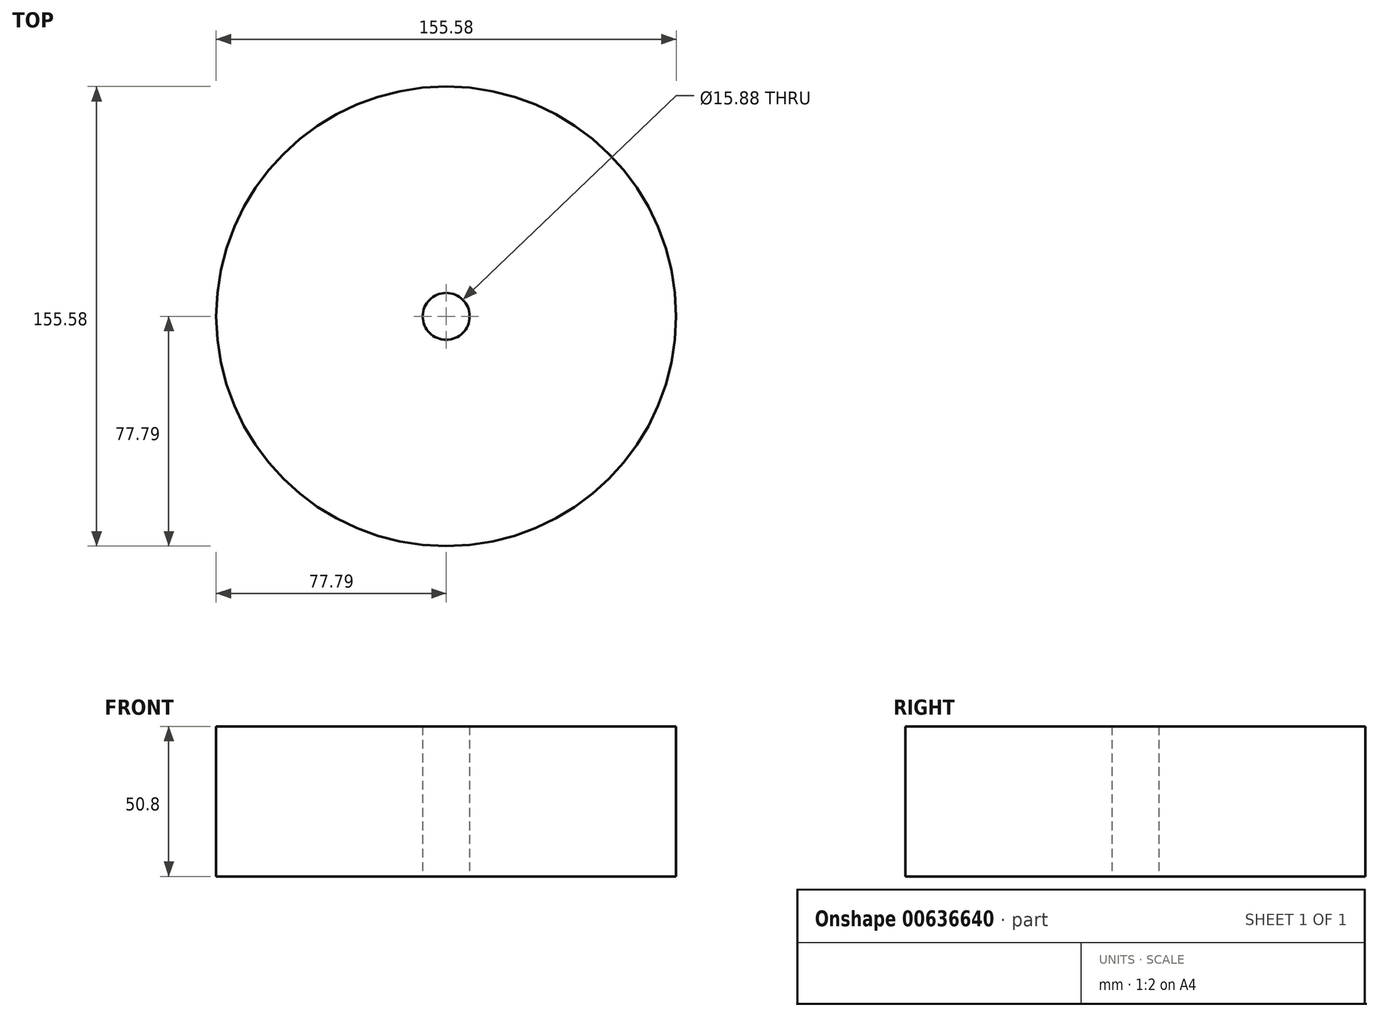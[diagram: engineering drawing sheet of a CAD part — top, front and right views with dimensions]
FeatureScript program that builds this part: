
annotation { "Feature Type Name" : "Feature", "Feature Type Description" : "" }
export const myFeature = defineFeature(function(context is Context, id is Id, definition is map)
    precondition{}
    {
        {
            var Q0;
            Q0=qCreatedBy(makeId("Top.planeOp"),FACE);
            var sketch = newSketch(context, id + "F0", { "sketchPlane" : qUnion([Q0])});
            skCircle(sketch, "E0", {"center": v(0, 0) * mm, "radius": 77.79 * mm});
            skCircle(sketch, "E1", {"center": v(0, 0) * mm, "radius": 7.94 * mm});
            skSolve(sketch);
        }
        {
            var Q0;
            Q0 = qSketchRegion(id + "F0", true);
            extrude(context, id + "F1", {"entities" : qUnion([Q0]), "depth" : 50.8 * mm, "offsetDistance" : 25.4 * mm});
        }
    });
